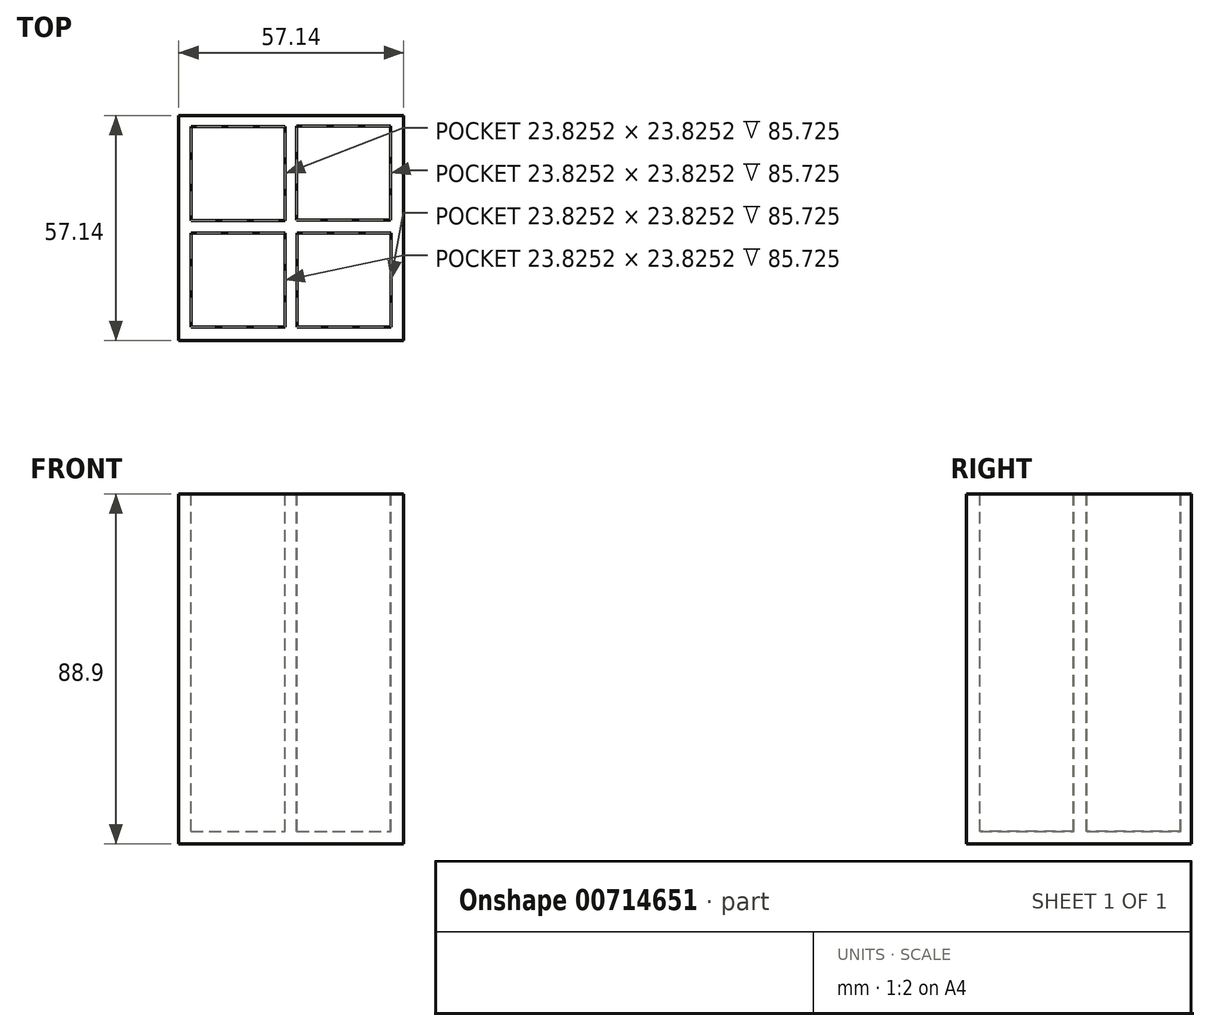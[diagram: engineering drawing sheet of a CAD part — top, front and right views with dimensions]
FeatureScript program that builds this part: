
annotation { "Feature Type Name" : "Feature", "Feature Type Description" : "" }
export const myFeature = defineFeature(function(context is Context, id is Id, definition is map)
    precondition{}
    {
        {
            var Q0;
            Q0=qCreatedBy(makeId("Top.planeOp"),FACE);
            var sketch = newSketch(context, id + "F0", { "sketchPlane" : qUnion([Q0])});
            skLineSegment(sketch, "E0.bottom", {"start": v(28.58, -28.58) * mm, "end": v(-28.57, -28.58) * mm});
            skLineSegment(sketch, "E0.top", {"start": v(28.57, 28.58) * mm, "end": v(-28.58, 28.57) * mm});
            skLineSegment(sketch, "E0.left", {"start": v(28.58, -28.58) * mm, "end": v(28.57, 28.58) * mm});
            skLineSegment(sketch, "E0.right", {"start": v(-28.58, -28.58) * mm, "end": v(-28.58, 28.57) * mm});
            skPoint(sketch, "E0.middle", {"position": v(0, 0) * mm});
            skSolve(sketch);
        }
        {
            var Q0;
            Q0=makeQuery(id+"F0.imprint","IMPRINT",FACE,{"disambiguationData":[TD([[makeQuery(id+"F0.imprint","IMPRINT",EDGE,{"derivedFrom":sQuery(id+"F0.wireOp",EDGE,"E0.bottom")}),-1.0]])]});
            extrude(context, id + "F1", {"entities" : qUnion([Q0]), "depth" : 88.9 * mm, "offsetDistance" : 25.4 * mm});
        }
        {
            var Q0;
            Q0=makeQuery(id+"F1.opExtrude","CAP_FACE",FACE,{"disambiguationData":[OSD([sQuery(id+"F0.wireOp",EDGE,"E0.bottom"),sQuery(id+"F0.wireOp",EDGE,"E0.top"),sQuery(id+"F0.wireOp",EDGE,"E0.left"),sQuery(id+"F0.wireOp",EDGE,"E0.right")])],"isStart":false});
            var sketch = newSketch(context, id + "F2", { "sketchPlane" : qUnion([Q0])});
            skLineSegment(sketch, "E1.bottom", {"start": v(-25.43, -25.12) * mm, "end": v(-1.6, -25.12) * mm});
            skLineSegment(sketch, "E1.top", {"start": v(-25.43, -1.3) * mm, "end": v(-1.6, -1.3) * mm});
            skLineSegment(sketch, "E1.left", {"start": v(-25.43, -25.12) * mm, "end": v(-25.43, -1.3) * mm});
            skLineSegment(sketch, "E1.right", {"start": v(-1.6, -25.12) * mm, "end": v(-1.6, -1.3) * mm});
            skSolve(sketch);
        }
        {
            var Q0;
            Q0=makeQuery(id+"F2.imprint","IMPRINT",FACE,{"disambiguationData":[TD([[makeQuery(id+"F2.imprint","IMPRINT",EDGE,{"derivedFrom":sQuery(id+"F2.wireOp",EDGE,"E1.bottom")}),-1.0]])]});
            var sketch = newSketch(context, id + "F3", { "sketchPlane" : qUnion([Q0])});
            skLineSegment(sketch, "E2.bottom", {"start": v(-25.4, 25.76) * mm, "end": v(-1.58, 25.76) * mm});
            skLineSegment(sketch, "E2.top", {"start": v(-25.4, 1.93) * mm, "end": v(-1.58, 1.93) * mm});
            skLineSegment(sketch, "E2.left", {"start": v(-25.4, 25.76) * mm, "end": v(-25.4, 1.93) * mm});
            skLineSegment(sketch, "E2.right", {"start": v(-1.58, 25.76) * mm, "end": v(-1.58, 1.93) * mm});
            skSolve(sketch);
        }
        {
            var Q0;
            Q0=makeQuery(id+"F3.imprint","IMPRINT",FACE,{"disambiguationData":[TD([[makeQuery(id+"F3.imprint","IMPRINT",EDGE,{"derivedFrom":sQuery(id+"F3.wireOp",EDGE,"E2.bottom")}),1.0]])]});
            var sketch = newSketch(context, id + "F4", { "sketchPlane" : qUnion([Q0])});
            skLineSegment(sketch, "E3.bottom", {"start": v(1.34, 2.05) * mm, "end": v(25.17, 2.05) * mm});
            skLineSegment(sketch, "E3.top", {"start": v(1.34, 25.87) * mm, "end": v(25.17, 25.87) * mm});
            skLineSegment(sketch, "E3.left", {"start": v(1.34, 2.05) * mm, "end": v(1.34, 25.87) * mm});
            skLineSegment(sketch, "E3.right", {"start": v(25.17, 2.05) * mm, "end": v(25.17, 25.87) * mm});
            skSolve(sketch);
        }
        {
            var Q0;
            Q0=makeQuery(id+"F2.imprint","IMPRINT",FACE,{"disambiguationData":[TD([[makeQuery(id+"F2.imprint","IMPRINT",EDGE,{"derivedFrom":sQuery(id+"F2.wireOp",EDGE,"E1.bottom")}),-1.0]])]});
            var sketch = newSketch(context, id + "F5", { "sketchPlane" : qUnion([Q0])});
            skLineSegment(sketch, "E4.bottom", {"start": v(1.47, -1.33) * mm, "end": v(25.3, -1.33) * mm});
            skLineSegment(sketch, "E4.top", {"start": v(1.47, -25.16) * mm, "end": v(25.3, -25.16) * mm});
            skLineSegment(sketch, "E4.left", {"start": v(1.47, -1.33) * mm, "end": v(1.47, -25.16) * mm});
            skLineSegment(sketch, "E4.right", {"start": v(25.3, -1.33) * mm, "end": v(25.3, -25.16) * mm});
            skSolve(sketch);
        }
        {
            var Q0;
            Q0=makeQuery(id+"F3.imprint","IMPRINT",FACE,{"disambiguationData":[TD([[makeQuery(id+"F3.imprint","IMPRINT",EDGE,{"derivedFrom":sQuery(id+"F3.wireOp",EDGE,"E2.bottom")}),-1.0]])]});
            extrude(context, id + "F6", {"entities" : qUnion([Q0]), "operationType" : NewBodyOperationType.REMOVE, "oppositeDirection" : true, "depth" : 85.72 * mm, "offsetDistance" : 25.4 * mm});
        }
        {
            var Q0;
            Q0=makeQuery(id+"F4.imprint","IMPRINT",FACE,{"disambiguationData":[TD([[makeQuery(id+"F4.imprint","IMPRINT",EDGE,{"derivedFrom":sQuery(id+"F4.wireOp",EDGE,"E3.bottom")}),1.0]])]});
            extrude(context, id + "F7", {"entities" : qUnion([Q0]), "operationType" : NewBodyOperationType.REMOVE, "oppositeDirection" : true, "depth" : 85.72 * mm, "offsetDistance" : 25.4 * mm});
        }
        {
            var Q0;
            Q0=makeQuery(id+"F5.imprint","IMPRINT",FACE,{"disambiguationData":[TD([[makeQuery(id+"F5.imprint","IMPRINT",EDGE,{"derivedFrom":sQuery(id+"F5.wireOp",EDGE,"E4.bottom")}),-1.0]])]});
            extrude(context, id + "F8", {"entities" : qUnion([Q0]), "operationType" : NewBodyOperationType.REMOVE, "oppositeDirection" : true, "depth" : 85.72 * mm, "offsetDistance" : 25.4 * mm});
        }
        {
            var Q0;
            Q0=makeQuery(id+"F2.imprint","IMPRINT",FACE,{"disambiguationData":[TD([[makeQuery(id+"F2.imprint","IMPRINT",EDGE,{"derivedFrom":sQuery(id+"F2.wireOp",EDGE,"E1.bottom")}),1.0]])]});
            extrude(context, id + "F9", {"entities" : qUnion([Q0]), "operationType" : NewBodyOperationType.REMOVE, "oppositeDirection" : true, "depth" : 85.72 * mm, "offsetDistance" : 25.4 * mm});
        }
    });
